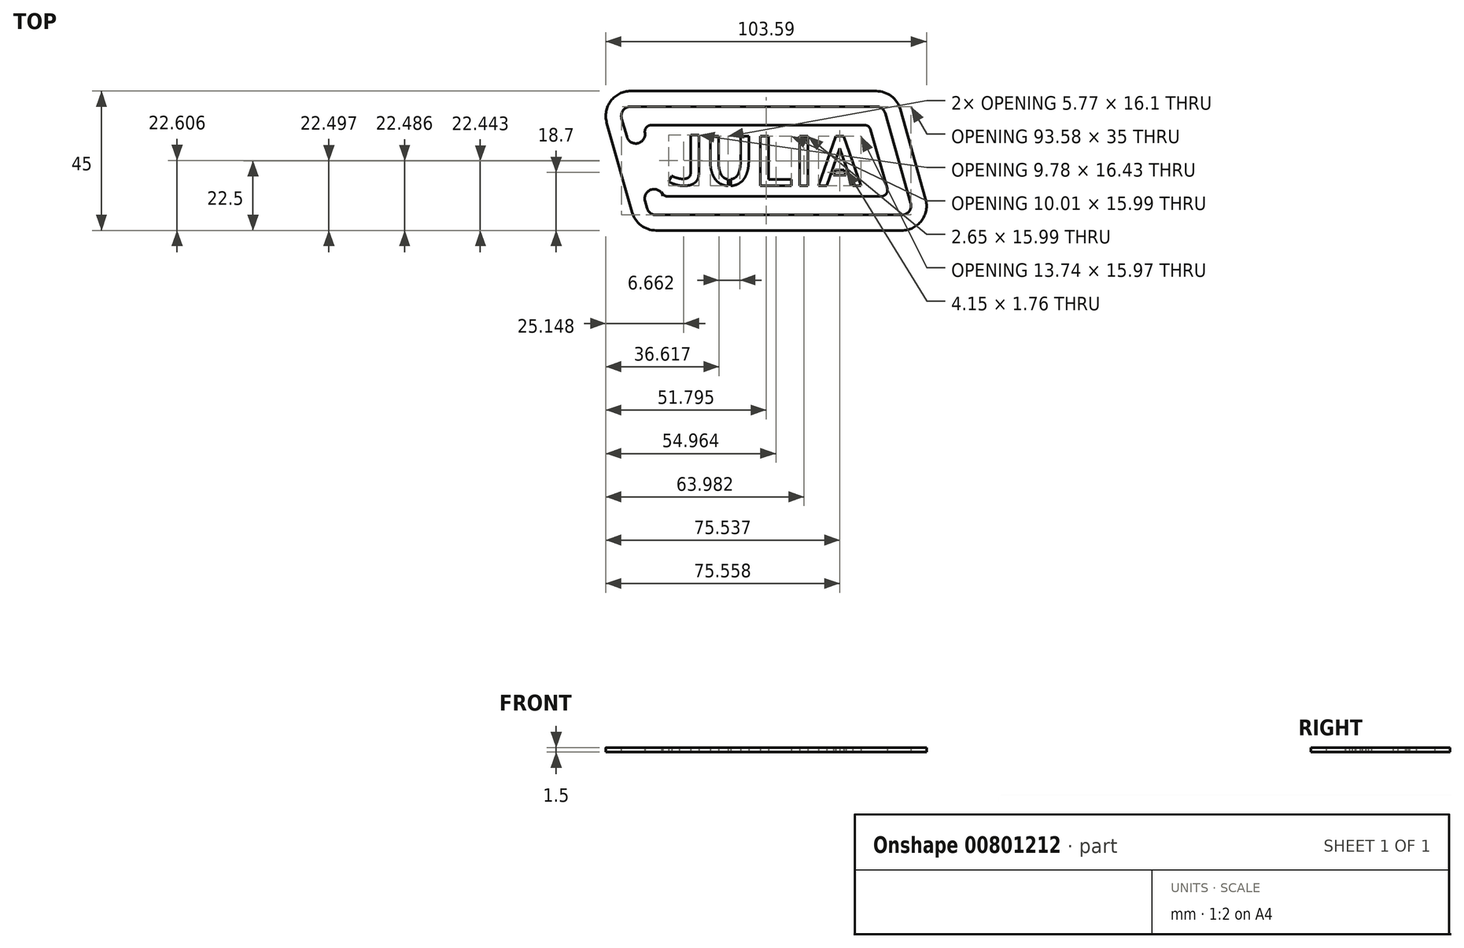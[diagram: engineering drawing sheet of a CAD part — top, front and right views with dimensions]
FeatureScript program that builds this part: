
annotation { "Feature Type Name" : "Feature", "Feature Type Description" : "" }
export const myFeature = defineFeature(function(context is Context, id is Id, definition is map)
    precondition{}
    {
        {
            var Q0;
            Q0=qCreatedBy(makeId("Top.planeOp"),FACE);
            var sketch = newSketch(context, id + "F0", { "sketchPlane" : qUnion([Q0])});
            skLineSegment(sketch, "E0.bottom", {"start": v(-2.17, 45) * mm, "end": v(77.2, 45) * mm});
            skLineSegment(sketch, "E0.top", {"start": v(6.05, 0) * mm, "end": v(85.42, 0) * mm});
            skLineSegment(sketch, "E0.left", {"start": v(-9.87, 34.82) * mm, "end": v(-1.65, 5.82) * mm});
            skLineSegment(sketch, "E0.right", {"start": v(84.9, 39.18) * mm, "end": v(93.12, 10.18) * mm});
            skPoint(sketch, "E1.visualSharp", {"position": v(83.25, 45) * mm});
            skArc(sketch, "E1.filletArc", {"start": v(84.9, 39.18) * mm, "mid": v(82.03, 43.38) * mm, "end": v(77.2, 45) * mm});
            skPoint(sketch, "E2.visualSharp", {"position": v(96, 0) * mm});
            skArc(sketch, "E2.filletArc", {"start": v(85.42, 0) * mm, "mid": v(91.8, 3.18) * mm, "end": v(93.12, 10.18) * mm});
            skPoint(sketch, "E3.visualSharp", {"position": v(-12.75, 45) * mm});
            skArc(sketch, "E3.filletArc", {"start": v(-2.17, 45) * mm, "mid": v(-8.55, 41.82) * mm, "end": v(-9.87, 34.82) * mm});
            skPoint(sketch, "E4.visualSharp", {"position": v(0, 0) * mm});
            skArc(sketch, "E4.filletArc", {"start": v(-1.65, 5.82) * mm, "mid": v(1.22, 1.62) * mm, "end": v(6.05, 0) * mm});
            skLineSegment(sketch, "E5.0", {"start": v(-2.17, 40) * mm, "end": v(77.2, 40) * mm});
            skArc(sketch, "E5.1", {"start": v(80.09, 37.82) * mm, "mid": v(79.01, 39.4) * mm, "end": v(77.2, 40) * mm});
            skArc(sketch, "E5.2", {"start": v(-2.17, 40) * mm, "mid": v(-4.56, 38.8) * mm, "end": v(-5.05, 36.18) * mm});
            skLineSegment(sketch, "E5.3", {"start": v(80.09, 37.82) * mm, "end": v(88.3, 8.82) * mm});
            skLineSegment(sketch, "E5.4", {"start": v(-5.05, 36.18) * mm, "end": v(-3.38, 30.26) * mm});
            skArc(sketch, "E5.5", {"start": v(3.16, 7.18) * mm, "mid": v(4.24, 5.6) * mm, "end": v(6.05, 5) * mm});
            skLineSegment(sketch, "E5.6", {"start": v(6.05, 5) * mm, "end": v(85.42, 5) * mm});
            skArc(sketch, "E5.7", {"start": v(85.42, 5) * mm, "mid": v(87.81, 6.2) * mm, "end": v(88.3, 8.82) * mm});
            skLineSegment(sketch, "E6.0", {"start": v(75.35, 32.55) * mm, "end": v(80.73, 13.55) * mm});
            skLineSegment(sketch, "E7.0", {"start": v(9.83, 11) * mm, "end": v(78.8, 11) * mm});
            skLineSegment(sketch, "E8.0", {"start": v(4.45, 34) * mm, "end": v(73.42, 34) * mm});
            skLineSegment(sketch, "E9.0", {"start": v(2.4, 31.9) * mm, "end": v(2.52, 31.45) * mm});
            skLineSegment(sketch, "E10", {"start": v(-5.76, 20.32) * mm, "end": v(89, 24.68) * mm, "construction": true});
            skLineSegment(sketch, "E11", {"start": v(7.9, 12.45) * mm, "end": v(8.28, 11.14) * mm});
            skLineSegment(sketch, "E12", {"start": v(-0.35, 28.08) * mm, "end": v(-0.35, 28.08) * mm});
            skLineSegment(sketch, "E13.MirrorCS", {"start": v(-2.04, 12.98) * mm, "end": v(5.96, 13.35) * mm});
            skLineSegment(sketch, "E14", {"start": v(2.5, 9.5) * mm, "end": v(3.16, 7.18) * mm});
            skLineSegment(sketch, "E15", {"start": v(5.25, 13.32) * mm, "end": v(5.25, 13.32) * mm});
            skPoint(sketch, "E16.newPointA", {"position": v(9.56, 13.52) * mm});
            skPoint(sketch, "E16.newPointB", {"position": v(8.22, 11.33) * mm});
            skArc(sketch, "E16.filletArc", {"start": v(8.28, 11.14) * mm, "mid": v(7.14, 12.76) * mm, "end": v(5.25, 13.32) * mm});
            skArc(sketch, "E17.filletArc", {"start": v(5.25, 13.32) * mm, "mid": v(2.96, 12.07) * mm, "end": v(2.5, 9.5) * mm});
            skPoint(sketch, "E18.newPointA", {"position": v(10.38, 3.73) * mm});
            skArc(sketch, "E18.filletArc", {"start": v(7.9, 12.45) * mm, "mid": v(8.62, 11.4) * mm, "end": v(9.83, 11) * mm});
            skArc(sketch, "E19.filletArc", {"start": v(78.8, 11) * mm, "mid": v(80.4, 11.8) * mm, "end": v(80.73, 13.55) * mm});
            skArc(sketch, "E20.filletArc", {"start": v(75.35, 32.55) * mm, "mid": v(74.63, 33.6) * mm, "end": v(73.42, 34) * mm});
            skPoint(sketch, "E21.newPointB", {"position": v(6.07, 18.93) * mm});
            skArc(sketch, "E21.filletArc", {"start": v(4.45, 34) * mm, "mid": v(2.85, 33.2) * mm, "end": v(2.52, 31.45) * mm});
            skPoint(sketch, "E22.visualSharp", {"position": v(-2.73, 27.97) * mm});
            skArc(sketch, "E22.filletArc", {"start": v(-3.38, 30.26) * mm, "mid": v(-2.24, 28.64) * mm, "end": v(-0.35, 28.08) * mm});
            skPoint(sketch, "E23.newPointA", {"position": v(8.87, 28.5) * mm});
            skArc(sketch, "E23.filletArc", {"start": v(-0.35, 28.08) * mm, "mid": v(1.95, 29.32) * mm, "end": v(2.4, 31.9) * mm});
            skText(sketch, "E24", { "text": "JULIA", "fontName": "AllertaStencil-Regular.ttf"});
            skPoint(sketch, "E25", {"position": v(41.63, 22.5) * mm});
            skLineSegment(sketch, "E26", {"start": v(37.52, 45) * mm, "end": v(45.73, 0) * mm, "construction": true});
            const initialGuessF0  = {"E24": [0.00952, 0.0145, 1, 0, 0.016]};
            skSetInitialGuess(sketch, initialGuessF0);
            skSolve(sketch);
        }
        {
            var Q0;
            Q0=makeQuery(id+"F0.imprint","IMPRINT",FACE,{"disambiguationData":[TD([[makeQuery(id+"F0.imprint","IMPRINT",EDGE,{"derivedFrom":sQuery(id+"F0.wireOp",EDGE,"E0.bottom")}),-1.0]])]});
            extrude(context, id + "F1", {"entities" : qUnion([Q0]), "depth" : 1.5 * mm, "offsetDistance" : 25 * mm});
        }
    });
